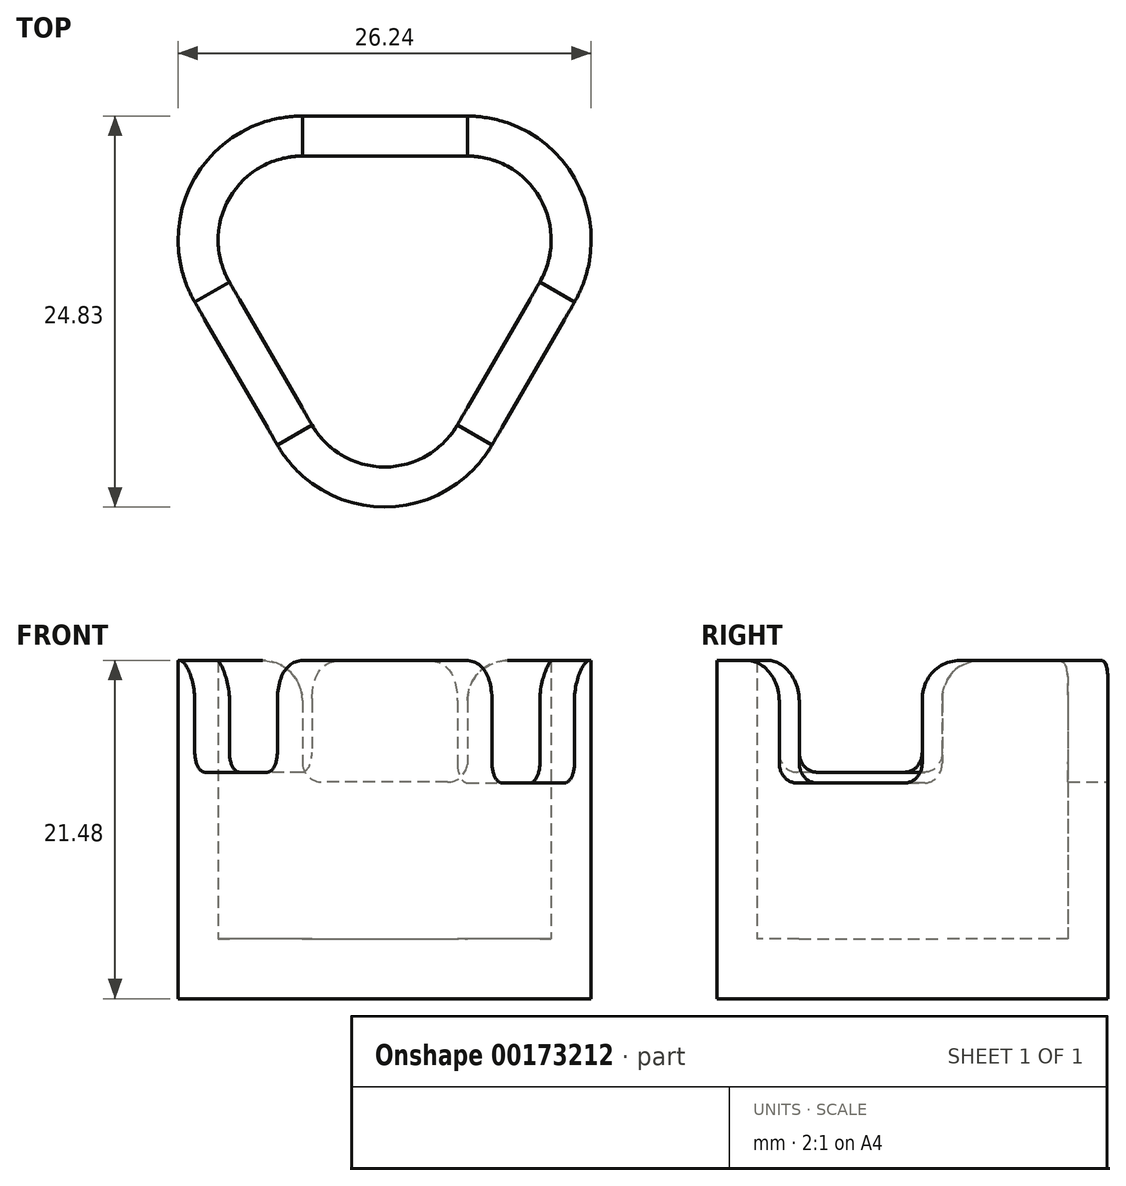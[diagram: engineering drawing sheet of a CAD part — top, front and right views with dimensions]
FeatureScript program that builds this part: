
annotation { "Feature Type Name" : "Feature", "Feature Type Description" : "" }
export const myFeature = defineFeature(function(context is Context, id is Id, definition is map)
    precondition{}
    {
        {
            var Q0;
            Q0=qCreatedBy(makeId("Top.planeOp"),FACE);
            var sketch = newSketch(context, id + "F0", { "sketchPlane" : qUnion([Q0])});
            skCircle(sketch, "E0", {"center": v(0, -6.06) * mm, "radius": 5.25 * mm});
            skCircle(sketch, "E1.MirrorC", {"center": v(-5.25, 3.03) * mm, "radius": 5.25 * mm});
            skCircle(sketch, "E2", {"center": v(5.25, 3.03) * mm, "radius": 5.25 * mm});
            skLineSegment(sketch, "E3", {"start": v(17.91, 3.01) * mm, "end": v(18, 3.01) * mm});
            skPoint(sketch, "E4.0.midPoint", {"position": v(18, 3.01) * mm});
            skCircle(sketch, "E5", {"center": v(0, 0) * mm, "radius": 11.31 * mm, "construction": true});
            skSolve(sketch);
        }
        {
            var Q0;
            Q0=qCreatedBy(makeId("Top.planeOp"),FACE);
            var sketch = newSketch(context, id + "F1", { "sketchPlane" : qUnion([Q0])});
            skLineSegment(sketch, "E6", {"start": v(-5.25, 8.36) * mm, "end": v(5.25, 8.36) * mm});
            skLineSegment(sketch, "E7", {"start": v(9.86, 0.37) * mm, "end": v(4.61, -8.73) * mm});
            skLineSegment(sketch, "E8", {"start": v(-4.61, -8.73) * mm, "end": v(-9.86, 0.37) * mm});
            skPoint(sketch, "E9.visualSharp", {"position": v(14.48, 8.36) * mm});
            skArc(sketch, "E9.filletArc", {"start": v(9.86, 0.37) * mm, "mid": v(9.86, 5.7) * mm, "end": v(5.25, 8.36) * mm});
            skPoint(sketch, "E10.visualSharp", {"position": v(-14.48, 8.36) * mm});
            skArc(sketch, "E10.filletArc", {"start": v(-5.25, 8.36) * mm, "mid": v(-9.86, 5.7) * mm, "end": v(-9.86, 0.37) * mm});
            skPoint(sketch, "E11.visualSharp", {"position": v(0, -16.72) * mm});
            skArc(sketch, "E11.filletArc", {"start": v(-4.61, -8.73) * mm, "mid": v(0, -11.39) * mm, "end": v(4.61, -8.73) * mm});
            skArc(sketch, "E12.0", {"start": v(12.06, -0.9) * mm, "mid": v(12.06, 6.96) * mm, "end": v(5.25, 10.9) * mm});
            skArc(sketch, "E13.0", {"start": v(-5.25, 10.9) * mm, "mid": v(-12.06, 6.96) * mm, "end": v(-12.06, -0.9) * mm});
            skArc(sketch, "E14.0", {"start": v(-6.81, -10) * mm, "mid": v(0, -13.93) * mm, "end": v(6.81, -10) * mm});
            skLineSegment(sketch, "E15", {"start": v(-12.06, -0.9) * mm, "end": v(-6.81, -10) * mm});
            skLineSegment(sketch, "E16", {"start": v(6.81, -10) * mm, "end": v(12.06, -0.9) * mm});
            skLineSegment(sketch, "E17", {"start": v(5.25, 10.9) * mm, "end": v(-5.25, 10.9) * mm});
            skSolve(sketch);
        }
        {
            var Q0;
            Q0=makeQuery(id+"F1.imprint","IMPRINT",FACE,{"disambiguationData":[TD([[makeQuery(id+"F1.imprint","IMPRINT",EDGE,{"derivedFrom":sQuery(id+"F1.wireOp",EDGE,"E8")}),1.0]])]});
            var Q1;
            Q1=makeQuery(id+"F1.imprint","IMPRINT",FACE,{"disambiguationData":[TD([[makeQuery(id+"F1.imprint","IMPRINT",EDGE,{"derivedFrom":sQuery(id+"F1.wireOp",EDGE,"E7")}),1.0]])]});
            var Q2;
            Q2=makeQuery(id+"F1.imprint","IMPRINT",FACE,{"disambiguationData":[TD([[makeQuery(id+"F1.imprint","IMPRINT",EDGE,{"derivedFrom":sQuery(id+"F1.wireOp",EDGE,"E6")}),1.0]])]});
            extrude(context, id + "F2", {"entities" : qUnion([Q0, Q1, Q2]), "depth" : 17.67 * mm});
        }
        {
            var Q0;
            Q0=makeQuery(id+"F1.imprint","IMPRINT",FACE,{"disambiguationData":[TD([[makeQuery(id+"F1.imprint","IMPRINT",EDGE,{"derivedFrom":sQuery(id+"F1.wireOp",EDGE,"E6")}),-1.0]])]});
            var Q1;
            Q1=makeQuery(id+"F1.imprint","IMPRINT",FACE,{"disambiguationData":[TD([[makeQuery(id+"F1.imprint","IMPRINT",EDGE,{"derivedFrom":sQuery(id+"F1.wireOp",EDGE,"E11.filletArc")}),-1.0]])]});
            var Q2;
            Q2=makeQuery(id+"F1.imprint","IMPRINT",FACE,{"disambiguationData":[TD([[makeQuery(id+"F1.imprint","IMPRINT",EDGE,{"derivedFrom":sQuery(id+"F1.wireOp",EDGE,"E9.filletArc")}),-1.0]])]});
            var Q3;
            Q3=makeQuery(id+"F1.imprint","IMPRINT",FACE,{"disambiguationData":[TD([[makeQuery(id+"F1.imprint","IMPRINT",EDGE,{"derivedFrom":sQuery(id+"F1.wireOp",EDGE,"E7")}),1.0]])]});
            var Q4;
            Q4=makeQuery(id+"F1.imprint","IMPRINT",FACE,{"disambiguationData":[TD([[makeQuery(id+"F1.imprint","IMPRINT",EDGE,{"derivedFrom":sQuery(id+"F1.wireOp",EDGE,"E8")}),1.0]])]});
            var Q5;
            Q5=makeQuery(id+"F1.imprint","IMPRINT",FACE,{"disambiguationData":[TD([[makeQuery(id+"F1.imprint","IMPRINT",EDGE,{"derivedFrom":sQuery(id+"F1.wireOp",EDGE,"E10.filletArc")}),-1.0]])]});
            var Q6;
            Q6=makeQuery(id+"F1.imprint","IMPRINT",FACE,{"disambiguationData":[TD([[makeQuery(id+"F1.imprint","IMPRINT",EDGE,{"derivedFrom":sQuery(id+"F1.wireOp",EDGE,"E6")}),1.0]])]});
            extrude(context, id + "F3", {"entities" : qUnion([Q0, Q1, Q2, Q3, Q4, Q5, Q6]), "operationType" : NewBodyOperationType.ADD, "oppositeDirection" : true, "depth" : 3.8 * mm});
        }
        {
            var Q0;
            Q0=makeQuery(id+"F2.opExtrude","SWEPT_FACE",FACE,{"disambiguationData":[OSD([sQuery(id+"F1.wireOp",EDGE,"E15")])]});
            cPlane(context, id + "F4", {"entities" : qUnion([Q0]), "cplaneType" : CPlaneType.OFFSET, "offset" : 25.4 * mm, "width" : 152.4 * mm, "height" : 152.4 * mm});
        }
        {
            var Q0;
            Q0=qCreatedBy(id+"F4.planeOp",FACE);
            var sketch = newSketch(context, id + "F5", { "sketchPlane" : qUnion([Q0])});
            skLineSegment(sketch, "E18", {"start": v(-5.24, 18.35) * mm, "end": v(5.25, 18.35) * mm});
            skLineSegment(sketch, "E19", {"start": v(5.25, 18.35) * mm, "end": v(5.25, 10.57) * mm});
            skLineSegment(sketch, "E20", {"start": v(5.25, 10.57) * mm, "end": v(-5.24, 10.57) * mm});
            skLineSegment(sketch, "E21", {"start": v(-5.24, 10.57) * mm, "end": v(-5.24, 18.35) * mm});
            skSolve(sketch);
        }
        {
            var Q0;
            Q0=makeQuery(id+"F5.imprint","IMPRINT",FACE,{"disambiguationData":[TD([[makeQuery(id+"F5.imprint","IMPRINT",EDGE,{"derivedFrom":sQuery(id+"F5.wireOp",EDGE,"E18")}),-1.0]])]});
            extrude(context, id + "F6", {"entities" : qUnion([Q0]), "operationType" : NewBodyOperationType.REMOVE, "oppositeDirection" : true, "depth" : 30.18 * mm});
        }
        {
            var Q0;
            {var subQ0=sQuery(id+"F1.wireOp",EDGE,"E17");Q0=makeQuery(id+"F3.boolean.opBoolean","MERGE",FACE,{"derivedFrom":[makeQuery(id+"F2.opExtrude","SWEPT_FACE",FACE,{"disambiguationData":[OSD([subQ0])]}),makeQuery(id+"F3.opExtrude","SWEPT_FACE",FACE,{"disambiguationData":[OSD([subQ0])]})]});}
            cPlane(context, id + "F7", {"entities" : qUnion([Q0]), "cplaneType" : CPlaneType.OFFSET, "offset" : 25.4 * mm, "width" : 152.4 * mm, "height" : 152.4 * mm});
        }
        {
            var Q0;
            Q0=qCreatedBy(id+"F7.planeOp",FACE);
            var sketch = newSketch(context, id + "F8", { "sketchPlane" : qUnion([Q0])});
            skLineSegment(sketch, "E22.bottom", {"start": v(-5.26, 17.72) * mm, "end": v(5.23, 17.72) * mm});
            skLineSegment(sketch, "E22.top", {"start": v(-5.26, 9.94) * mm, "end": v(5.23, 9.94) * mm});
            skLineSegment(sketch, "E22.left", {"start": v(-5.26, 17.72) * mm, "end": v(-5.26, 9.94) * mm});
            skLineSegment(sketch, "E22.right", {"start": v(5.23, 17.72) * mm, "end": v(5.23, 9.94) * mm});
            skSolve(sketch);
        }
        {
            var Q0;
            Q0=makeQuery(id+"F8.imprint","IMPRINT",FACE,{"disambiguationData":[TD([[makeQuery(id+"F8.imprint","IMPRINT",EDGE,{"derivedFrom":sQuery(id+"F8.wireOp",EDGE,"E22.bottom")}),-1.0]])]});
            extrude(context, id + "F9", {"entities" : qUnion([Q0]), "operationType" : NewBodyOperationType.REMOVE, "oppositeDirection" : true, "depth" : 32 * mm});
        }
        {
            var Q0;
            {var subQ0=sQuery(id+"F1.wireOp",EDGE,"E16");Q0=makeQuery(id+"F3.boolean.opBoolean","MERGE",FACE,{"derivedFrom":[makeQuery(id+"F2.opExtrude","SWEPT_FACE",FACE,{"disambiguationData":[OSD([subQ0])]}),makeQuery(id+"F3.opExtrude","SWEPT_FACE",FACE,{"disambiguationData":[OSD([subQ0])]})]});}
            cPlane(context, id + "F10", {"entities" : qUnion([Q0]), "cplaneType" : CPlaneType.OFFSET, "offset" : 25.4 * mm, "width" : 152.4 * mm, "height" : 152.4 * mm});
        }
        {
            var Q0;
            Q0=qCreatedBy(id+"F10.planeOp",FACE);
            var sketch = newSketch(context, id + "F11", { "sketchPlane" : qUnion([Q0])});
            skLineSegment(sketch, "E23.bottom", {"start": v(-5.24, 17.67) * mm, "end": v(5.24, 17.67) * mm});
            skLineSegment(sketch, "E23.top", {"start": v(-5.24, 9.9) * mm, "end": v(5.24, 9.9) * mm});
            skLineSegment(sketch, "E23.left", {"start": v(-5.24, 17.67) * mm, "end": v(-5.24, 9.9) * mm});
            skLineSegment(sketch, "E23.right", {"start": v(5.24, 17.67) * mm, "end": v(5.24, 9.9) * mm});
            skSolve(sketch);
        }
        {
            var Q0;
            Q0=makeQuery(id+"F11.imprint","IMPRINT",FACE,{"disambiguationData":[TD([[makeQuery(id+"F11.imprint","IMPRINT",EDGE,{"derivedFrom":sQuery(id+"F11.wireOp",EDGE,"E23.bottom")}),-1.0]])]});
            extrude(context, id + "F12", {"entities" : qUnion([Q0]), "operationType" : NewBodyOperationType.REMOVE, "oppositeDirection" : true, "depth" : 31.67 * mm});
        }
        {
            var Q0;
            Q0=makeQuery(id+"F9.boolean.opBoolean","INTERSECT",EDGE,{"derivedFrom":[makeQuery(id+"F2.opExtrude","CAP_FACE",FACE,{"disambiguationData":[OSD([sQuery(id+"F1.wireOp",EDGE,"E6"),sQuery(id+"F1.wireOp",EDGE,"E7"),sQuery(id+"F1.wireOp",EDGE,"E8"),sQuery(id+"F1.wireOp",EDGE,"E9.filletArc"),sQuery(id+"F1.wireOp",EDGE,"E10.filletArc"),sQuery(id+"F1.wireOp",EDGE,"E11.filletArc"),sQuery(id+"F1.wireOp",EDGE,"E12.0"),sQuery(id+"F1.wireOp",EDGE,"E13.0"),sQuery(id+"F1.wireOp",EDGE,"E14.0"),sQuery(id+"F1.wireOp",EDGE,"E15"),sQuery(id+"F1.wireOp",EDGE,"E16"),sQuery(id+"F1.wireOp",EDGE,"E17")])],"isStart":false}),makeQuery(id+"F9.opExtrude","SWEPT_FACE",FACE,{"disambiguationData":[OSD([sQuery(id+"F8.wireOp",EDGE,"E22.left")])]})]});
            var Q1;
            Q1=makeQuery(id+"F9.boolean.opBoolean","INTERSECT",EDGE,{"derivedFrom":[makeQuery(id+"F2.opExtrude","CAP_FACE",FACE,{"disambiguationData":[OSD([sQuery(id+"F1.wireOp",EDGE,"E6"),sQuery(id+"F1.wireOp",EDGE,"E7"),sQuery(id+"F1.wireOp",EDGE,"E8"),sQuery(id+"F1.wireOp",EDGE,"E9.filletArc"),sQuery(id+"F1.wireOp",EDGE,"E10.filletArc"),sQuery(id+"F1.wireOp",EDGE,"E11.filletArc"),sQuery(id+"F1.wireOp",EDGE,"E12.0"),sQuery(id+"F1.wireOp",EDGE,"E13.0"),sQuery(id+"F1.wireOp",EDGE,"E14.0"),sQuery(id+"F1.wireOp",EDGE,"E15"),sQuery(id+"F1.wireOp",EDGE,"E16"),sQuery(id+"F1.wireOp",EDGE,"E17")])],"isStart":false}),makeQuery(id+"F9.opExtrude","SWEPT_FACE",FACE,{"disambiguationData":[OSD([sQuery(id+"F8.wireOp",EDGE,"E22.right")])]})]});
            var Q2;
            {var subQ0=sQuery(id+"F1.wireOp",EDGE,"E16");var subQ1=sQuery(id+"F1.wireOp",EDGE,"E15");var subQ2=sQuery(id+"F1.wireOp",EDGE,"E14.0");var subQ3=sQuery(id+"F1.wireOp",EDGE,"E12.0");var subQ4=sQuery(id+"F1.wireOp",EDGE,"E11.filletArc");var subQ5=sQuery(id+"F1.wireOp",EDGE,"E7");var subQ6=sQuery(id+"F1.wireOp",EDGE,"E8");var subQ7=sQuery(id+"F1.wireOp",EDGE,"E9.filletArc");Q2=makeQuery(id+"F12.boolean.opBoolean","INTERSECT",EDGE,{"derivedFrom":[makeQuery(id+"F9.boolean.opBoolean","SPLIT",FACE,{"disambiguationData":[TD([makeQuery(id+"F2.opExtrude","SWEPT_FACE",FACE,{"disambiguationData":[OSD([subQ5])]})])],"derivedFrom":makeQuery(id+"F2.opExtrude","CAP_FACE",FACE,{"disambiguationData":[OSD([sQuery(id+"F1.wireOp",EDGE,"E6"),subQ5,subQ6,subQ7,sQuery(id+"F1.wireOp",EDGE,"E10.filletArc"),subQ4,subQ3,sQuery(id+"F1.wireOp",EDGE,"E13.0"),subQ2,subQ1,subQ0,sQuery(id+"F1.wireOp",EDGE,"E17")])],"isStart":false})}),makeQuery(id+"F12.opExtrude","SWEPT_FACE",FACE,{"disambiguationData":[OSD([sQuery(id+"F11.wireOp",EDGE,"E23.left")])]})]});}
            var Q3;
            {var subQ0=sQuery(id+"F1.wireOp",EDGE,"E16");var subQ1=sQuery(id+"F1.wireOp",EDGE,"E15");var subQ2=sQuery(id+"F1.wireOp",EDGE,"E14.0");var subQ3=sQuery(id+"F1.wireOp",EDGE,"E12.0");var subQ4=sQuery(id+"F1.wireOp",EDGE,"E11.filletArc");var subQ5=sQuery(id+"F1.wireOp",EDGE,"E7");var subQ6=sQuery(id+"F1.wireOp",EDGE,"E8");var subQ7=sQuery(id+"F1.wireOp",EDGE,"E9.filletArc");Q3=makeQuery(id+"F12.boolean.opBoolean","INTERSECT",EDGE,{"derivedFrom":[makeQuery(id+"F9.boolean.opBoolean","SPLIT",FACE,{"disambiguationData":[TD([makeQuery(id+"F2.opExtrude","SWEPT_FACE",FACE,{"disambiguationData":[OSD([subQ5])]})])],"derivedFrom":makeQuery(id+"F2.opExtrude","CAP_FACE",FACE,{"disambiguationData":[OSD([sQuery(id+"F1.wireOp",EDGE,"E6"),subQ5,subQ6,subQ7,sQuery(id+"F1.wireOp",EDGE,"E10.filletArc"),subQ4,subQ3,sQuery(id+"F1.wireOp",EDGE,"E13.0"),subQ2,subQ1,subQ0,sQuery(id+"F1.wireOp",EDGE,"E17")])],"isStart":false})}),makeQuery(id+"F12.opExtrude","SWEPT_FACE",FACE,{"disambiguationData":[OSD([sQuery(id+"F11.wireOp",EDGE,"E23.right")])]})]});}
            var Q4;
            Q4=makeQuery(id+"F6.boolean.opBoolean","INTERSECT",EDGE,{"derivedFrom":[makeQuery(id+"F2.opExtrude","CAP_FACE",FACE,{"disambiguationData":[OSD([sQuery(id+"F1.wireOp",EDGE,"E6"),sQuery(id+"F1.wireOp",EDGE,"E7"),sQuery(id+"F1.wireOp",EDGE,"E8"),sQuery(id+"F1.wireOp",EDGE,"E9.filletArc"),sQuery(id+"F1.wireOp",EDGE,"E10.filletArc"),sQuery(id+"F1.wireOp",EDGE,"E11.filletArc"),sQuery(id+"F1.wireOp",EDGE,"E12.0"),sQuery(id+"F1.wireOp",EDGE,"E13.0"),sQuery(id+"F1.wireOp",EDGE,"E14.0"),sQuery(id+"F1.wireOp",EDGE,"E15"),sQuery(id+"F1.wireOp",EDGE,"E16"),sQuery(id+"F1.wireOp",EDGE,"E17")])],"isStart":false}),makeQuery(id+"F6.opExtrude","SWEPT_FACE",FACE,{"disambiguationData":[OSD([sQuery(id+"F5.wireOp",EDGE,"E19")])]})]});
            var Q5;
            Q5=makeQuery(id+"F6.boolean.opBoolean","INTERSECT",EDGE,{"derivedFrom":[makeQuery(id+"F2.opExtrude","CAP_FACE",FACE,{"disambiguationData":[OSD([sQuery(id+"F1.wireOp",EDGE,"E6"),sQuery(id+"F1.wireOp",EDGE,"E7"),sQuery(id+"F1.wireOp",EDGE,"E8"),sQuery(id+"F1.wireOp",EDGE,"E9.filletArc"),sQuery(id+"F1.wireOp",EDGE,"E10.filletArc"),sQuery(id+"F1.wireOp",EDGE,"E11.filletArc"),sQuery(id+"F1.wireOp",EDGE,"E12.0"),sQuery(id+"F1.wireOp",EDGE,"E13.0"),sQuery(id+"F1.wireOp",EDGE,"E14.0"),sQuery(id+"F1.wireOp",EDGE,"E15"),sQuery(id+"F1.wireOp",EDGE,"E16"),sQuery(id+"F1.wireOp",EDGE,"E17")])],"isStart":false}),makeQuery(id+"F6.opExtrude","SWEPT_FACE",FACE,{"disambiguationData":[OSD([sQuery(id+"F5.wireOp",EDGE,"E21")])]})]});
            fillet(context, id + "F13", {"entities" : qUnion([Q0, Q1, Q2, Q3, Q4, Q5]), "radius" : 2.54 * mm, "tangentPropagation" : true, "allowEdgeOverflow" : false});
        }
        {
            var Q0;
            Q0=makeQuery(id+"F6.boolean.opBoolean","COPY",EDGE,{"derivedFrom":makeQuery(id+"F6.opExtrude","SWEPT_EDGE",EDGE,{"disambiguationData":[OSD([sQuery(id+"F5.wireOp",EDGE,"E19"),sQuery(id+"F5.wireOp",EDGE,"E20")])]})});
            var Q1;
            Q1=makeQuery(id+"F9.boolean.opBoolean","COPY",EDGE,{"derivedFrom":makeQuery(id+"F9.opExtrude","SWEPT_EDGE",EDGE,{"disambiguationData":[OSD([sQuery(id+"F8.wireOp",EDGE,"E22.top"),sQuery(id+"F8.wireOp",EDGE,"E22.left")])]})});
            var Q2;
            Q2=makeQuery(id+"F9.boolean.opBoolean","COPY",EDGE,{"derivedFrom":makeQuery(id+"F9.opExtrude","SWEPT_EDGE",EDGE,{"disambiguationData":[OSD([sQuery(id+"F8.wireOp",EDGE,"E22.top"),sQuery(id+"F8.wireOp",EDGE,"E22.right")])]})});
            var Q3;
            Q3=makeQuery(id+"F12.boolean.opBoolean","COPY",EDGE,{"derivedFrom":makeQuery(id+"F12.opExtrude","SWEPT_EDGE",EDGE,{"disambiguationData":[OSD([sQuery(id+"F11.wireOp",EDGE,"E23.top"),sQuery(id+"F11.wireOp",EDGE,"E23.left")])]})});
            var Q4;
            Q4=makeQuery(id+"F12.boolean.opBoolean","COPY",EDGE,{"derivedFrom":makeQuery(id+"F12.opExtrude","SWEPT_EDGE",EDGE,{"disambiguationData":[OSD([sQuery(id+"F11.wireOp",EDGE,"E23.top"),sQuery(id+"F11.wireOp",EDGE,"E23.right")])]})});
            var Q5;
            Q5=makeQuery(id+"F6.boolean.opBoolean","COPY",EDGE,{"derivedFrom":makeQuery(id+"F6.opExtrude","SWEPT_EDGE",EDGE,{"disambiguationData":[OSD([sQuery(id+"F5.wireOp",EDGE,"E20"),sQuery(id+"F5.wireOp",EDGE,"E21")])]})});
            fillet(context, id + "F14", {"entities" : qUnion([Q0, Q1, Q2, Q3, Q4, Q5]), "radius" : 1.27 * mm, "tangentPropagation" : true, "allowEdgeOverflow" : false});
        }
    });
